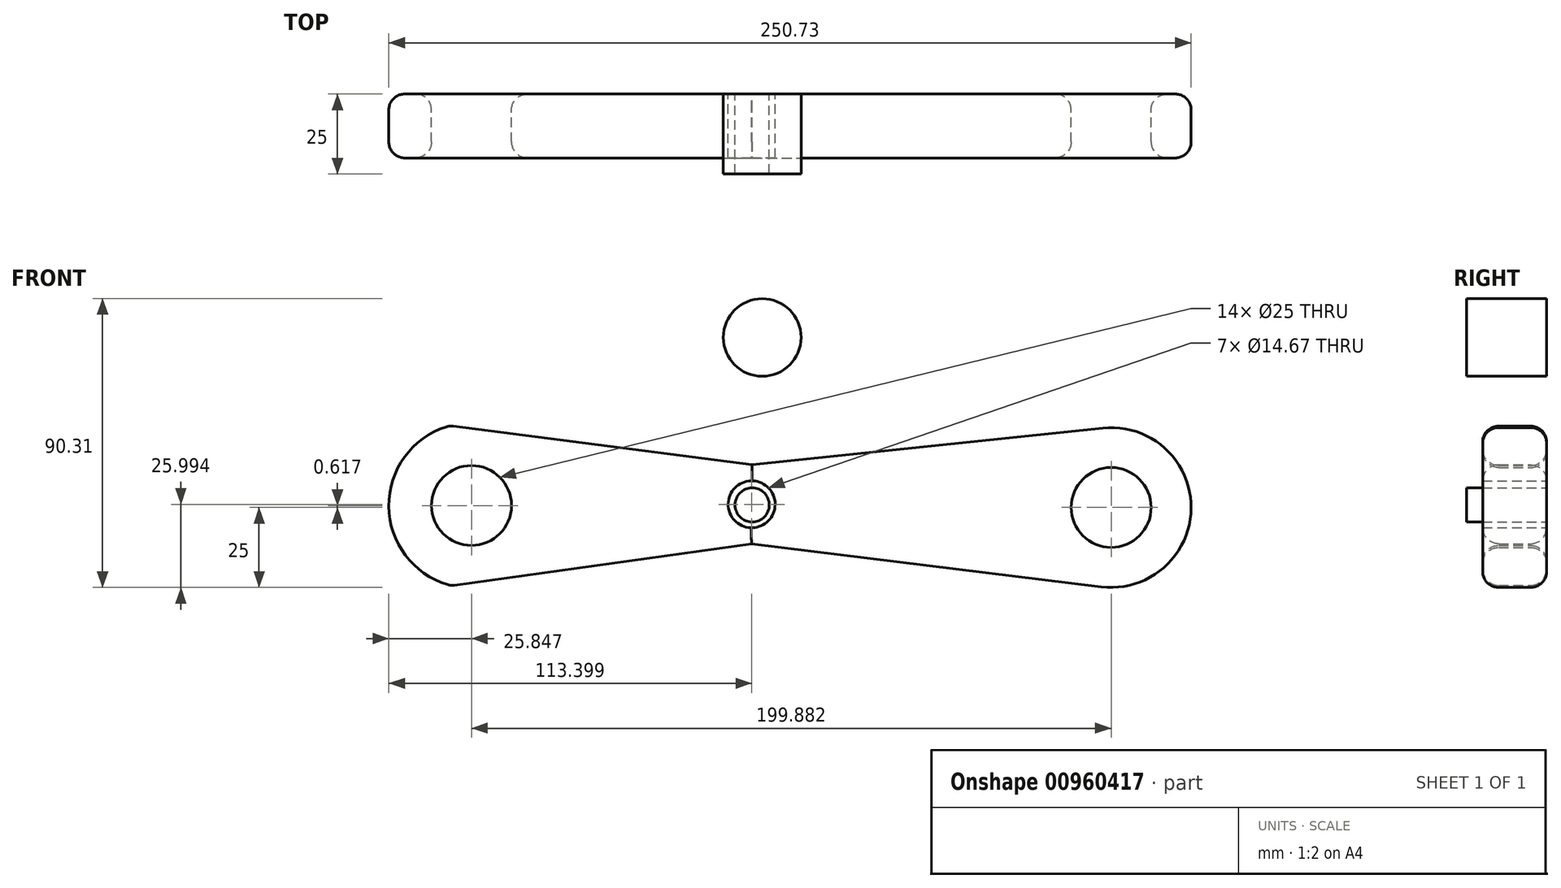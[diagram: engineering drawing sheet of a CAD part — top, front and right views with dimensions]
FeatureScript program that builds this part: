
annotation { "Feature Type Name" : "Feature", "Feature Type Description" : "" }
export const myFeature = defineFeature(function(context is Context, id is Id, definition is map)
    precondition{}
    {
        {
            var Q0;
            Q0=qCreatedBy(makeId("Front.planeOp"),FACE);
            var sketch = newSketch(context, id + "F0", { "sketchPlane" : qUnion([Q0])});
            skLineSegment(sketch, "E0", {"start": v(-71.98, 25.56) * mm, "end": v(22.5, 13.33) * mm});
            skLineSegment(sketch, "E1", {"start": v(-71.57, -24.44) * mm, "end": v(22.28, -11.34) * mm});
            skArc(sketch, "E2", {"start": v(-71.98, 25.56) * mm, "mid": v(-91.06, 0.4) * mm, "end": v(-71.57, -24.44) * mm});
            skCircle(sketch, "E3", {"center": v(22.34, 1) * mm, "radius": 7.33 * mm});
            skCircle(sketch, "E4", {"center": v(-65.21, 0.62) * mm, "radius": 0.22 * mm});
            skLineSegment(sketch, "E5", {"start": v(22.5, 13.33) * mm, "end": v(132.05, 24.86) * mm});
            skLineSegment(sketch, "E6", {"start": v(22.28, -11.34) * mm, "end": v(131.61, -24.81) * mm});
            skArc(sketch, "E7", {"start": v(131.61, -24.81) * mm, "mid": v(159.67, -0.22) * mm, "end": v(132.05, 24.86) * mm});
            skCircle(sketch, "E8", {"center": v(-65.21, 0.62) * mm, "radius": 12.5 * mm});
            skCircle(sketch, "E9", {"center": v(134.67, 0) * mm, "radius": 12.5 * mm});
            skCircle(sketch, "E10", {"center": v(22.34, 1) * mm, "radius": 5.97 * mm});
            skSolve(sketch);
        }
        {
            var Q0;
            Q0 = qSketchRegion(id + "F0", true);
            extrude(context, id + "F1", {"entities" : qUnion([Q0]), "depth" : 20 * mm, "offsetDistance" : 25.4 * mm});
        }
        {
            var Q0;
            Q0=makeQuery(id+"F1.opExtrude","CAP_EDGE",EDGE,{"disambiguationData":[OSD([sQuery(id+"F0.wireOp",EDGE,"E0")])],"isStart":false});
            var Q1;
            Q1=makeQuery(id+"F1.opExtrude","CAP_EDGE",EDGE,{"disambiguationData":[OSD([sQuery(id+"F0.wireOp",EDGE,"E5")])],"isStart":false});
            var Q2;
            Q2=makeQuery(id+"F1.opExtrude","CAP_EDGE",EDGE,{"disambiguationData":[OSD([sQuery(id+"F0.wireOp",EDGE,"E1")])],"isStart":false});
            var Q3;
            Q3=makeQuery(id+"F1.opExtrude","CAP_EDGE",EDGE,{"disambiguationData":[OSD([sQuery(id+"F0.wireOp",EDGE,"E2")])],"isStart":false});
            var Q4;
            Q4=makeQuery(id+"F1.opExtrude","CAP_EDGE",EDGE,{"disambiguationData":[OSD([sQuery(id+"F0.wireOp",EDGE,"E0")])],"isStart":true});
            var Q5;
            Q5=makeQuery(id+"F1.opExtrude","CAP_EDGE",EDGE,{"disambiguationData":[OSD([sQuery(id+"F0.wireOp",EDGE,"E5")])],"isStart":true});
            var Q6;
            Q6=makeQuery(id+"F1.opExtrude","CAP_EDGE",EDGE,{"disambiguationData":[OSD([sQuery(id+"F0.wireOp",EDGE,"E1")])],"isStart":true});
            var Q7;
            Q7=makeQuery(id+"F1.opExtrude","SWEPT_FACE",FACE,{"disambiguationData":[OSD([sQuery(id+"F0.wireOp",EDGE,"E2")])]});
            var Q8;
            Q8=makeQuery(id+"F1.opExtrude","CAP_EDGE",EDGE,{"disambiguationData":[OSD([sQuery(id+"F0.wireOp",EDGE,"E8")])],"isStart":false});
            var Q9;
            Q9=makeQuery(id+"F1.opExtrude","CAP_EDGE",EDGE,{"disambiguationData":[OSD([sQuery(id+"F0.wireOp",EDGE,"E8")])],"isStart":true});
            var Q10;
            Q10=makeQuery(id+"F1.opExtrude","CAP_EDGE",EDGE,{"disambiguationData":[OSD([sQuery(id+"F0.wireOp",EDGE,"E9")])],"isStart":false});
            var Q11;
            Q11=makeQuery(id+"F1.opExtrude","CAP_EDGE",EDGE,{"disambiguationData":[OSD([sQuery(id+"F0.wireOp",EDGE,"E9")])],"isStart":true});
            fillet(context, id + "F2", {"entities" : qUnion([Q0, Q1, Q2, Q3, Q4, Q5, Q6, Q7, Q8, Q9, Q10, Q11]), "radius" : 5 * mm, "tangentPropagation" : true, "allowEdgeOverflow" : false});
        }
        {
            var Q0;
            Q0=qCreatedBy(makeId("Front.planeOp"),FACE);
            var sketch = newSketch(context, id + "F3", { "sketchPlane" : qUnion([Q0])});
            skCircle(sketch, "E11", {"center": v(22.5, 0.8) * mm, "radius": 5.34 * mm});
            skSolve(sketch);
        }
        {
            var Q0;
            Q0=makeQuery(id+"F3.imprint","IMPRINT",FACE,{"disambiguationData":[TD([[makeQuery(id+"F3.imprint","IMPRINT",EDGE,{"derivedFrom":sQuery(id+"F3.wireOp",EDGE,"E11")}),1.0]])]});
            extrude(context, id + "F4", {"entities" : qUnion([Q0]), "depth" : 25 * mm, "offsetDistance" : 25 * mm});
        }
        {
            var Q0;
            Q0=qCreatedBy(makeId("Front.planeOp"),FACE);
            var sketch = newSketch(context, id + "F5", { "sketchPlane" : qUnion([Q0])});
            skCircle(sketch, "E12", {"center": v(25.63, 53.18) * mm, "radius": 12.13 * mm});
            skSolve(sketch);
        }
        {
            var Q0;
            Q0=makeQuery(id+"F5.imprint","IMPRINT",FACE,{"disambiguationData":[TD([[makeQuery(id+"F5.imprint","IMPRINT",EDGE,{"derivedFrom":sQuery(id+"F5.wireOp",EDGE,"E12")}),1.0]])]});
            extrude(context, id + "F6", {"entities" : qUnion([Q0]), "depth" : 25 * mm, "offsetDistance" : 25 * mm});
        }
    });
